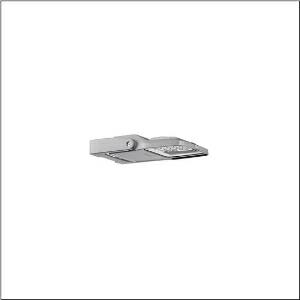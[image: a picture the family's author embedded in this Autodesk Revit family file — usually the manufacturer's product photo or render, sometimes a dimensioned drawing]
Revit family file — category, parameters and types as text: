
# Revit family: floodlight_fl_21_micro___pl61_5xa7762a4c2a_6f7d
name_source: partatom
category: Lighting Fixtures
units: mm (PartAtom-declared; Revit-internal decimal feet)

## family parameters
Cut with Voids When Loaded = No
Host = Face
Light Source = No
Part Type = Normal
Room Calculation Point = No
Round Connector Dimension = Use Diameter
Shared = No

## types (1)
- --- (1 x LED, 3030 lm, 23.1 W, 4000K)
    Apparent Load = 23 VA
    CIE Flux Codes = 33 65 98 100 100
    Color Rendering = 70
    Color Temperature = 4000K
    Default Elevation = 1800 mm
    Description = Floodlight FL 21 micro, floodlight, primary light control with lens, of PMMA, primary optical cover: protective disc, of toughened safety glass, transparent, light distribution: PL61, light emission: direct distribution, installation type: surface-mounted, LED, High Power LED, rated luminous flux: 3.030lm, luminous efficacy: 131lm/W, light colour: 740, colour temperature: 4000K, control gear: ECG iQ, control: Auto-Match, Temp-Guard, Night-Set, Smart-Wire, Desk-Remote (wireless, voltage-free reading and setting of iQ features in the workshop via application-optimized NFC function/RFID function), optimised constant luminous flux control (CLO 2.0), Street-Remote, with terminal, 6-pole, mains connection: 220..240V, AC, 50/60Hz, start of lifetime: 23W, end of lifetime: 24W, reduction: 11W, luminaire housing, of diecast aluminium, powder-coated, Siteco® metallic grey (DB 702S), corrosivity category C5 according to DIN EN ISO 12944, design bracket, of diecast aluminium, powder-coated, Siteco® metallic grey (DB 702S), protection rating (complete): IP66, insulation class (complete): insulation class II (safety insulation), certification: CE, protection symbol: D, impact resistance: IK07, permissible operating ambient temperature: -40..+40°C, permissible operating ambient temperature for outdoor applications: -40..+50°C, standard: DIN EN 12944, packaging unit: 1 piece

Light Distribution: PL61
    Height = 65 mm
    Lamp = 1 x LED
    Lamp Light Flux = 3030 lm
    Lamp Power = 23.1 W
    Lamp count = 1
    Length = 312 mm
    Luminous efficacy = 131 lm/W
    Manufacturer = Siteco
    ModVariant = No
    Model = 5XA7762A4C2A
    Number of Poles = 1
    OnlyDefault = Yes
    Power Factor = 1
    Product Name = Floodlight FL 21 micro | PL61
    Product group = floodlight | pylon top
    ProductGroupID = 6101
    Protection Class = Protection class II
    Protection Degree = IP 66
    RLX_Detail_Level = 1
    RlxData = <blob elided: 97293 chars, md5=4340ced6>
    Socket = socket
    Standby Power = 0 W
    System Light Flux = 3030 lm
    System Power = 23 W
    Type Comments = factory setting: luminous flux: 100 % | dim-lin: 254 | 455 mA
    Type Image = l_1006878.jpg
    URL = http://relux.com
    VarID = @adj_115219
    Voltage = 0 V
    Weight = 0.00 kg
    Width = 230 mm

## geometry (parser evidence)
native form markers: Blend x4, Sweep x11
no freeform markers — native parametric forms only
